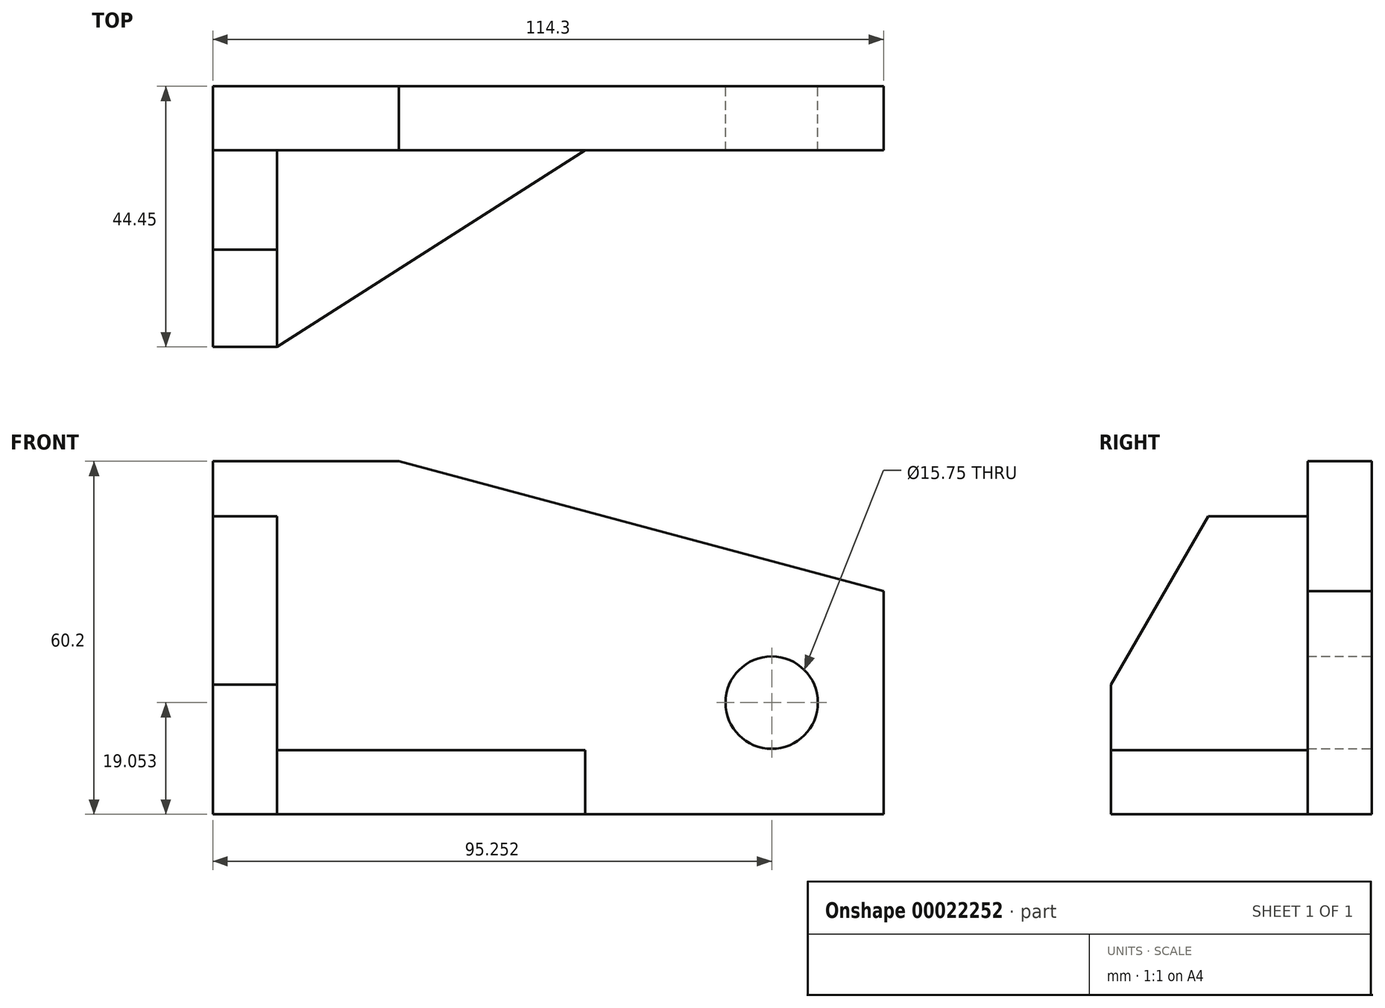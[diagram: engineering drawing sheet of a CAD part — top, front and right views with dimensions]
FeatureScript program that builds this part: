
annotation { "Feature Type Name" : "Feature", "Feature Type Description" : "" }
export const myFeature = defineFeature(function(context is Context, id is Id, definition is map)
    precondition{}
    {
        {
            var Q0;
            Q0=qCreatedBy(makeId("Front.planeOp"),FACE);
            var sketch = newSketch(context, id + "F0", { "sketchPlane" : qUnion([Q0])});
            skLineSegment(sketch, "E0.bottom", {"start": v(-55.96, 20.02) * mm, "end": v(-24.2, 20.02) * mm});
            skLineSegment(sketch, "E0.top", {"start": v(-55.96, -40.18) * mm, "end": v(58.34, -40.18) * mm});
            skLineSegment(sketch, "E0.left", {"start": v(-55.96, 20.02) * mm, "end": v(-55.96, -40.18) * mm});
            skLineSegment(sketch, "E0.right", {"start": v(58.34, -2.1) * mm, "end": v(58.34, -40.18) * mm});
            skLineSegment(sketch, "E1", {"start": v(-24.2, 20.02) * mm, "end": v(58.34, -2.1) * mm});
            skCircle(sketch, "E2", {"center": v(39.3, -21.13) * mm, "radius": 7.87 * mm});
            skSolve(sketch);
        }
        {
            var Q0;
            Q0 = qSketchRegion(id + "F0", true);
            extrude(context, id + "F1", {"entities" : qUnion([Q0]), "depth" : 10.92 * mm});
        }
        {
            var Q0;
            Q0=makeQuery(id+"F1.opExtrude","CAP_FACE",FACE,{"disambiguationData":[OSD([sQuery(id+"F0.wireOp",EDGE,"E0.bottom"),sQuery(id+"F0.wireOp",EDGE,"E0.top"),sQuery(id+"F0.wireOp",EDGE,"E0.left"),sQuery(id+"F0.wireOp",EDGE,"E0.right"),sQuery(id+"F0.wireOp",EDGE,"E1"),sQuery(id+"F0.wireOp",EDGE,"E2")])],"isStart":false});
            var sketch = newSketch(context, id + "F2", { "sketchPlane" : qUnion([Q0])});
            skLineSegment(sketch, "E3.bottom", {"start": v(-55.96, -40.18) * mm, "end": v(-45.04, -40.18) * mm});
            skLineSegment(sketch, "E3.top", {"start": v(-55.96, 10.62) * mm, "end": v(-45.04, 10.62) * mm});
            skLineSegment(sketch, "E3.left", {"start": v(-55.96, -40.18) * mm, "end": v(-55.96, 10.62) * mm});
            skLineSegment(sketch, "E3.right", {"start": v(-45.04, -40.18) * mm, "end": v(-45.04, 10.62) * mm});
            skSolve(sketch);
        }
        {
            var Q0;
            Q0 = qSketchRegion(id + "F2", true);
            extrude(context, id + "F3", {"entities" : qUnion([Q0]), "operationType" : NewBodyOperationType.ADD, "depth" : 33.53 * mm});
        }
        {
            var Q0;
            Q0=makeQuery(id+"F3.opExtrude","SWEPT_FACE",FACE,{"disambiguationData":[OSD([sQuery(id+"F2.wireOp",EDGE,"E3.right")])]});
            var sketch = newSketch(context, id + "F4", { "sketchPlane" : qUnion([Q0])});
            skLineSegment(sketch, "E4", {"start": v(-27.88, 10.62) * mm, "end": v(-44.45, -18.08) * mm});
            skSolve(sketch);
        }
        {
            var Q0;
            {var subQ2=sQuery(id+"F4.wireOp",EDGE,"E4");Q0=makeQuery(id+"F4.imprint","IMPRINT",FACE,{"disambiguationData":[TD([[makeQuery(id+"F4.imprint","IMPRINT",EDGE,{"derivedFrom":subQ2}),-1.0]])]});}
            extrude(context, id + "F5", {"entities" : qUnion([Q0]), "operationType" : NewBodyOperationType.REMOVE, "oppositeDirection" : true, "depth" : 25.4 * mm});
        }
        {
            var Q0;
            Q0=makeQuery(id+"F1.opExtrude","CAP_FACE",FACE,{"disambiguationData":[OSD([sQuery(id+"F0.wireOp",EDGE,"E0.bottom"),sQuery(id+"F0.wireOp",EDGE,"E0.top"),sQuery(id+"F0.wireOp",EDGE,"E0.left"),sQuery(id+"F0.wireOp",EDGE,"E0.right"),sQuery(id+"F0.wireOp",EDGE,"E1"),sQuery(id+"F0.wireOp",EDGE,"E2")])],"isStart":false});
            var sketch = newSketch(context, id + "F6", { "sketchPlane" : qUnion([Q0])});
            skLineSegment(sketch, "E5.bottom", {"start": v(-45.04, -40.18) * mm, "end": v(7.54, -40.18) * mm});
            skLineSegment(sketch, "E5.top", {"start": v(-45.04, -29.26) * mm, "end": v(7.54, -29.26) * mm});
            skLineSegment(sketch, "E5.left", {"start": v(-45.04, -40.18) * mm, "end": v(-45.04, -29.26) * mm});
            skLineSegment(sketch, "E5.right", {"start": v(7.54, -40.18) * mm, "end": v(7.54, -29.26) * mm});
            skSolve(sketch);
        }
        {
            var Q0;
            Q0=makeQuery(id+"F6.imprint","IMPRINT",FACE,{"disambiguationData":[TD([[makeQuery(id+"F6.imprint","IMPRINT",EDGE,{"derivedFrom":sQuery(id+"F6.wireOp",EDGE,"E5.bottom")}),1.0]])]});
            extrude(context, id + "F7", {"entities" : qUnion([Q0]), "operationType" : NewBodyOperationType.ADD, "depth" : 33.53 * mm});
        }
        {
            var Q0;
            Q0=makeQuery(id+"F7.opExtrude","SWEPT_FACE",FACE,{"disambiguationData":[OSD([sQuery(id+"F6.wireOp",EDGE,"E5.top")])]});
            var sketch = newSketch(context, id + "F8", { "sketchPlane" : qUnion([Q0])});
            skLineSegment(sketch, "E6", {"start": v(7.54, -10.92) * mm, "end": v(-45.04, -44.45) * mm});
            skSolve(sketch);
        }
        {
            var Q0;
            Q0=makeQuery(id+"F8.imprint","IMPRINT",FACE,{"disambiguationData":[TD([[makeQuery(id+"F8.imprint","IMPRINT",EDGE,{"derivedFrom":sQuery(id+"F8.wireOp",EDGE,"E6")}),1.0]])]});
            extrude(context, id + "F9", {"entities" : qUnion([Q0]), "operationType" : NewBodyOperationType.REMOVE, "endBound" : BoundingType.THROUGH_ALL, "oppositeDirection" : true, "depth" : 25.4 * mm});
        }
    });
